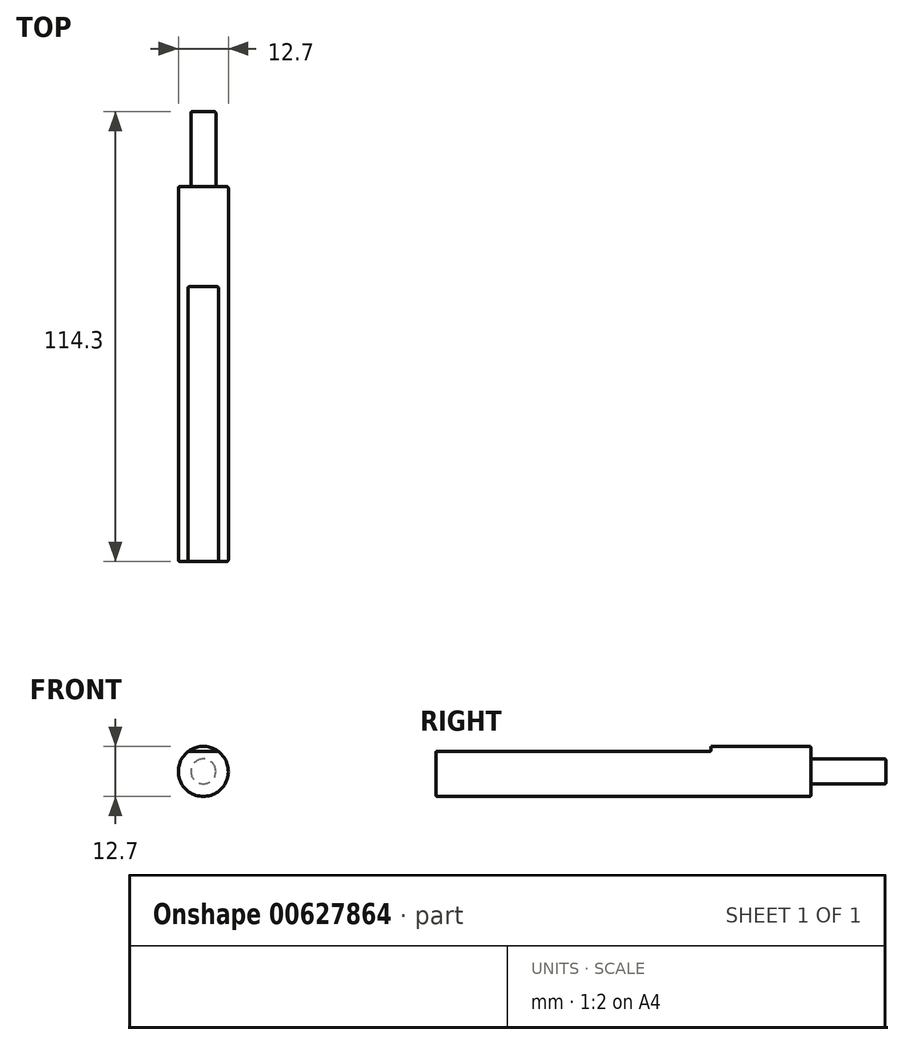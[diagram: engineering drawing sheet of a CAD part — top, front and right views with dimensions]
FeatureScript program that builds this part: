
annotation { "Feature Type Name" : "Feature", "Feature Type Description" : "" }
export const myFeature = defineFeature(function(context is Context, id is Id, definition is map)
    precondition{}
    {
        {
            var Q0;
            Q0=qCreatedBy(makeId("Right.planeOp"),FACE);
            var sketch = newSketch(context, id + "F0", { "sketchPlane" : qUnion([Q0])});
            skLineSegment(sketch, "E0", {"start": v(74.41, 3.18) * mm, "end": v(55.36, 3.18) * mm});
            skLineSegment(sketch, "E1", {"start": v(55.36, 3.17) * mm, "end": v(55.36, 6.35) * mm});
            skLineSegment(sketch, "E2", {"start": v(55.36, 6.35) * mm, "end": v(-39.89, 6.35) * mm});
            skLineSegment(sketch, "E3", {"start": v(-39.89, 6.35) * mm, "end": v(-39.89, 0) * mm});
            skLineSegment(sketch, "E4", {"start": v(-39.89, 0) * mm, "end": v(74.41, 0) * mm});
            skLineSegment(sketch, "E5", {"start": v(74.41, 0) * mm, "end": v(74.41, 3.18) * mm});
            skSolve(sketch);
        }
        {
            var Q0;
            Q0=makeQuery(id+"F0.imprint","IMPRINT",FACE,{"disambiguationData":[TD([[makeQuery(id+"F0.imprint","IMPRINT",EDGE,{"derivedFrom":sQuery(id+"F0.wireOp",EDGE,"E0")}),1.0]])]});
            var Q1;
            Q1=sQuery(id+"F0.wireOp",EDGE,"E4");
            revolve(context, id + "F1", {"entities" : qUnion([Q0]), "axis" : qUnion([Q1]), "revolveType" : RevolveType.FULL});
        }
        {
            var Q0;
            Q0=makeQuery(id+"F1.opRevolve","SWEPT_FACE",FACE,{"disambiguationData":[OSD([sQuery(id+"F0.wireOp",EDGE,"E3")])]});
            var sketch = newSketch(context, id + "F2", { "sketchPlane" : qUnion([Q0])});
            skPoint(sketch, "E6", {"position": v(3.88, 5.03) * mm});
            skPoint(sketch, "E7", {"position": v(-3.88, 5.03) * mm});
            skLineSegment(sketch, "E8", {"start": v(-3.88, 5.03) * mm, "end": v(3.88, 5.03) * mm});
            skSolve(sketch);
        }
        {
            var Q0;
            Q0 = qSketchRegion(id + "F2", true);
            var Q1;
            {var subQ0=sQuery(id+"F2.wireOp",EDGE,"E8");Q1=makeQuery(id+"F2.imprint","IMPRINT",FACE,{"disambiguationData":[TD([[makeQuery(id+"F2.imprint","IMPRINT",EDGE,{"derivedFrom":subQ0}),1.0]])]});}
            extrude(context, id + "F3", {"entities" : qUnion([Q0, Q1]), "operationType" : NewBodyOperationType.REMOVE, "oppositeDirection" : true, "depth" : 69.85 * mm, "offsetDistance" : 25.4 * mm});
        }
        {
            var Q0;
            Q0=makeQuery(id+"F1.opRevolve","SWEPT_EDGE",EDGE,{"disambiguationData":[OSD([sQuery(id+"F0.wireOp",EDGE,"E1"),sQuery(id+"F0.wireOp",EDGE,"E2")])]});
            var Q1;
            Q1=makeQuery(id+"F1.opRevolve","SWEPT_FACE",FACE,{"disambiguationData":[OSD([sQuery(id+"F0.wireOp",EDGE,"E0")])]});
            fillet(context, id + "F4", {"entities" : qUnion([Q0, Q1]), "radius" : 0.38 * mm, "tangentPropagation" : true, "allowEdgeOverflow" : false});
        }
        {
            var Q0;
            Q0=makeQuery(id+"F1.opRevolve","SWEPT_EDGE",EDGE,{"disambiguationData":[OSD([sQuery(id+"F0.wireOp",EDGE,"E2"),sQuery(id+"F0.wireOp",EDGE,"E3")])]});
            fillet(context, id + "F5", {"entities" : qUnion([Q0]), "radius" : 0.38 * mm, "tangentPropagation" : true, "allowEdgeOverflow" : false});
        }
        {
            var Q0;
            Q0=makeQuery(id+"F3.boolean.opBoolean","COPY",EDGE,{"derivedFrom":makeQuery(id+"F3.opExtrude","CAP_EDGE",EDGE,{"disambiguationData":[OSD([sQuery(id+"F2.wireOp",EDGE,"E8")])],"isStart":false})});
            fillet(context, id + "F6", {"entities" : qUnion([Q0]), "radius" : 0.38 * mm, "tangentPropagation" : true, "allowEdgeOverflow" : false});
        }
    });
